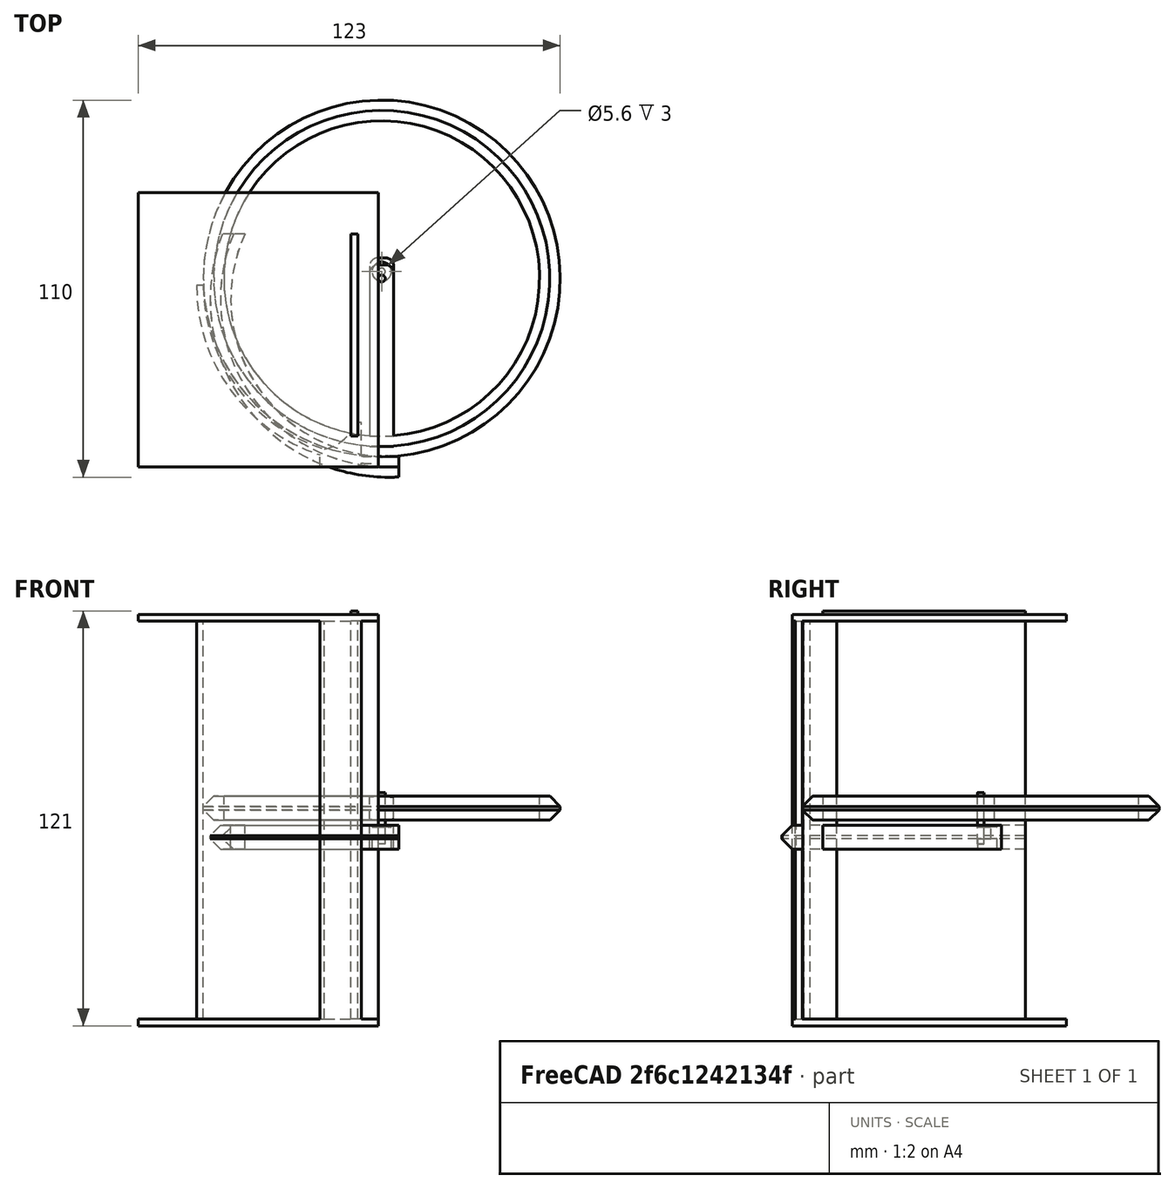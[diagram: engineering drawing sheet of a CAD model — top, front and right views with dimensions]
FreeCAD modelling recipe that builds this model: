
FCSTD DOCUMENT  (FreeCAD 0.17R13528 (Git))
Label: Hopper_v10A
License: All rights reserved
LicenseURL: http://en.wikipedia.org/wiki/All_rights_reserved
objects: Part::Cylinder×13, Part::Box×9, Part::Cut×8, Part::MultiFuse×7, Part::Chamfer×3, Part::Fillet×3, Part::MultiCommon×2, Part::Cone×1
note: 46 computed .brp shape members not serialized (recipe doc carries the construction recipe); baked Part::Feature solids carry a one-line shape summary decoded from their .brp

FEATURE [Part::Cylinder] Cylinder003
  Angle = 360
  AttacherType = Attacher::AttachEngine3D
  Height = 120
  Placement = pos=(0,0,-60) rot=(0,0,1;0rad)
  Radius = 50
FEATURE [Part::Cylinder] Cylinder004
  Angle = 360
  AttacherType = Attacher::AttachEngine3D
  Height = 120
  Placement = pos=(0,0,-60) rot=(0,0,1;0rad)
  Radius = 52
FEATURE [Part::Cut] Cut001
  Base = -> Cylinder004
  Tool = -> Cylinder003
FEATURE [Part::Box] Box002  label="Cube002"
  AttacherType = Attacher::AttachEngine3D
  Height = 120
  Length = 70
  Placement = pos=(-69,-70,-60) rot=(0,0,1;0rad)
  Width = 70
FEATURE [Part::MultiCommon] Common001
  Placement = pos=(0,-10,0) rot=(0,0,1;0rad)
  Shapes = -> [Cut001,Box002]
FEATURE [Part::Box] Box003  label="Cube003"
  AttacherType = Attacher::AttachEngine3D
  Height = 120
  Length = 2
  Placement = pos=(-7,-54,-59) rot=(0,0,1;0rad)
  Width = 59
FEATURE [Part::MultiFuse] Fusion007002
  Shapes = -> [Common001,Box003]
FEATURE [Part::Box] Box004  label="Cube004"
  AttacherType = Attacher::AttachEngine3D
  Height = 2
  Length = 70
  Placement = pos=(-69,-63,-60) rot=(0,0,1;0rad)
  Width = 80
FEATURE [Part::Box] Box005  label="Cube005"
  AttacherType = Attacher::AttachEngine3D
  Height = 2
  Length = 70
  Placement = pos=(-69,-63,58) rot=(0,0,1;0rad)
  Width = 80
FEATURE [Part::MultiFuse] Fusion007003
  Shapes = -> [Box005,Box004,Fusion007002]
FEATURE [Part::Cylinder] Cylinder007
  Angle = 360
  AttacherType = Attacher::AttachEngine3D
  Height = 120
  Placement = pos=(-17,-46,-60) rot=(0,0,1;0rad)
  Radius = 12
FEATURE [Part::Box] Box009  label="Cube008"
  AttacherType = Attacher::AttachEngine3D
  Height = 120
  Length = 12
  Placement = pos=(-16,-63,-60) rot=(0,0,1;0rad)
  Width = 13
FEATURE [Part::Cut] Cut003
  Base = -> Box009
  Tool = -> Cylinder007
FEATURE [Part::MultiFuse] Fusion007006  label="curve"
  Placement = pos=(-2,6,0) rot=(0,0,1;0rad)
  Shapes = -> [Fusion007003,Cut003]
FEATURE [Part::Cylinder] Cylinder
  Angle = 360
  AttacherType = Attacher::AttachEngine3D
  Height = 7
  Radius = 52
FEATURE [Part::Cylinder] Cylinder001
  Angle = 360
  AttacherType = Attacher::AttachEngine3D
  Height = 7
  Radius = 46
FEATURE [Part::Chamfer] Chamfer
  Base = -> Cylinder
  Edges = 2 edges r=3: [Edge1,Edge3]
FEATURE [Part::Cut] Cut
  Base = -> Chamfer
  Placement = pos=(8,2,0) rot=(0,0,1;0rad)
  Tool = -> Cylinder001
FEATURE [Part::Box] Box  label="Cube"
  AttacherType = Attacher::AttachEngine3D
  Height = 7
  Length = 52
  Placement = pos=(-4,-3.5,0) rot=(0,0,1;0rad)
  Width = 7
FEATURE [Part::Cylinder] Cylinder002  label="pinion_donotprint"
  Angle = 360
  AttacherType = Attacher::AttachEngine3D
  Height = 15
  Placement = pos=(0,0,-7) rot=(0,0,1;0rad)
  Radius = 1
FEATURE [Part::Fillet] Fillet
  Base = -> Box
  Edges = 2 edges r=2.4: [Edge1,Edge3]
FEATURE [Part::MultiFuse] Fusion
  Shapes = -> [Cut,Fillet]
FEATURE [Part::Box] Box001  label="Cube001"
  AttacherType = Attacher::AttachEngine3D
  Height = 10
  Length = 72
  Placement = pos=(-11,-65,-1) rot=(0,0,1;0rad)
  Width = 70
FEATURE [Part::MultiCommon] Common  label="arm000"
  Placement = pos=(0,0,-8.5) rot=(0,0,-1;0.785398rad)
  Shapes = -> [Box001,Fusion]
FEATURE [Part::Cylinder] Cylinder014
  Angle = 360
  AttacherType = Attacher::AttachEngine3D
  Height = 3
  Placement = pos=(0,0,-8.5) rot=(0,0,1;0rad)
  Radius = 2.8
FEATURE [Part::Cylinder] Cylinder016
  Angle = 360
  AttacherType = Attacher::AttachEngine3D
  Height = 1
  Placement = pos=(0,0,-2) rot=(0,0,1;0rad)
  Radius = 2.8
FEATURE [Part::MultiFuse] Fusion007016
  Shapes = -> [Cylinder016,Cylinder014]
FEATURE [Part::Cut] Cut012  label="arm004"
  Base = -> Common
  Tool = -> Fusion007016
FEATURE [Part::Cut] Cut014  label="arm006"
  Base = -> Cut012
  Placement = pos=(0,0,0) rot=(0,0,-1;0.785398rad)
  Tool = -> Cylinder002
FEATURE [Part::Cone] Cone005
  Angle = 360
  AttacherType = Attacher::AttachEngine3D
  Height = 1
  Placement = pos=(-57,10,-5) rot=(-1,0,0;1.5708rad)
  Radius1 = 0.1
  Radius2 = 2
FEATURE [Part::Cut] Cut025  label="arm"
  Base = -> Cut014
  Tool = -> Cone005
FEATURE [Part::Cylinder] Cylinder017
  Angle = 360
  AttacherType = Attacher::AttachEngine3D
  Height = 7
  Placement = pos=(2,-8,0) rot=(0,0,1;0rad)
  Radius = 52
FEATURE [Part::Cylinder] Cylinder018
  Angle = 360
  AttacherType = Attacher::AttachEngine3D
  Height = 7
  Placement = pos=(2,-8,0) rot=(0,0,1;0rad)
  Radius = 46
FEATURE [Part::Box] Box010  label="Cube009"
  AttacherType = Attacher::AttachEngine3D
  Height = 7
  Length = 53
  Placement = pos=(-4,-3.5,0) rot=(0,0,1;0rad)
  Width = 7
FEATURE [Part::Chamfer] Chamfer001
  Base = -> Cylinder017
  Edges = 2 edges r=3: [Edge1,Edge3]
FEATURE [Part::Fillet] Fillet001
  Base = -> Box010
  Edges = 2 edges r=2.4: [Edge1,Edge3]
  Placement = pos=(2,-8,0) rot=(0,0,1;0rad)
FEATURE [Part::Cut] Cut026
  Base = -> Chamfer001
  Tool = -> Cylinder018
FEATURE [Part::MultiFuse] Fusion007017
  Placement = pos=(8,0,0) rot=(0,0,1;4.71239rad)
  Shapes = -> [Cut026,Fillet001]
FEATURE [Part::Cylinder] Cylinder019  label="pinion_donotprint001"
  Angle = 360
  AttacherType = Attacher::AttachEngine3D
  Height = 15
  Placement = pos=(0,-2,-7) rot=(0,0,1;0rad)
  Radius = 1
FEATURE [Part::Box] Box011  label="Cube010"
  AttacherType = Attacher::AttachEngine3D
  Height = 7
  Length = 53
  Placement = pos=(-4,-3.5,0) rot=(0,0,1;0rad)
  Width = 7
FEATURE [Part::Cylinder] Cylinder020
  Angle = 360
  AttacherType = Attacher::AttachEngine3D
  Height = 7
  Placement = pos=(2,-8,0) rot=(0,0,1;0rad)
  Radius = 52
FEATURE [Part::Chamfer] Chamfer002
  Base = -> Cylinder020
  Edges = 2 edges r=3: [Edge1,Edge3]
FEATURE [Part::Fillet] Fillet002
  Base = -> Box011
  Edges = 2 edges r=2.4: [Edge1,Edge3]
  Placement = pos=(2,-8,0) rot=(0,0,1;0rad)
FEATURE [Part::Cylinder] Cylinder021
  Angle = 360
  AttacherType = Attacher::AttachEngine3D
  Height = 7
  Placement = pos=(2,-8,0) rot=(0,0,1;0rad)
  Radius = 46
FEATURE [Part::Cut] Cut027
  Base = -> Chamfer002
  Tool = -> Cylinder021
FEATURE [Part::MultiFuse] Fusion007018
  Placement = pos=(-2,6,0) rot=(0,0,1;0rad)
  Shapes = -> [Cut027,Fillet002]
